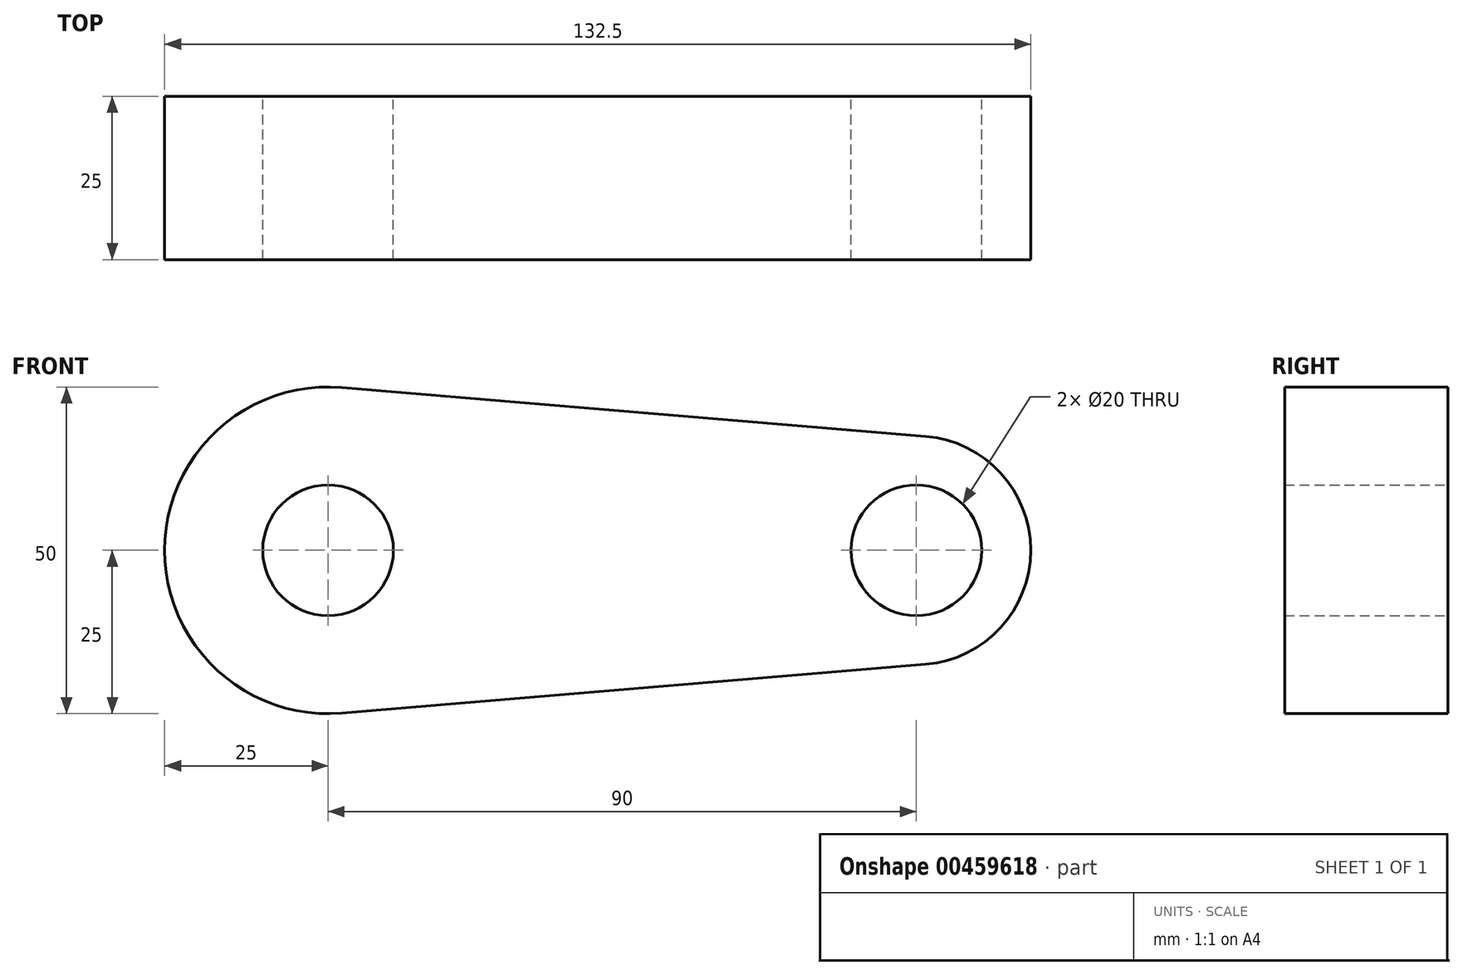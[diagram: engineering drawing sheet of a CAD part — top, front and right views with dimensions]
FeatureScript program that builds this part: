
annotation { "Feature Type Name" : "Feature", "Feature Type Description" : "" }
export const myFeature = defineFeature(function(context is Context, id is Id, definition is map)
    precondition{}
    {
        {
            var Q0;
            Q0=qCreatedBy(makeId("Front.planeOp"),FACE);
            var sketch = newSketch(context, id + "F0", { "sketchPlane" : qUnion([Q0])});
            skCircle(sketch, "E0", {"center": v(0, 0) * mm, "radius": 25 * mm});
            skCircle(sketch, "E1", {"center": v(90, 0) * mm, "radius": 17.5 * mm});
            skLineSegment(sketch, "E2", {"start": v(2.08, 24.91) * mm, "end": v(91.46, 17.44) * mm});
            skLineSegment(sketch, "E3", {"start": v(2.08, -24.91) * mm, "end": v(91.46, -17.44) * mm});
            skCircle(sketch, "E4", {"center": v(0, 0) * mm, "radius": 10 * mm});
            skCircle(sketch, "E5", {"center": v(90, 0) * mm, "radius": 10 * mm});
            skSolve(sketch);
        }
        {
            var Q0;
            Q0=makeQuery(id+"F0.imprint","IMPRINT",FACE,{"disambiguationData":[TD([[makeQuery(id+"F0.imprint","IMPRINT",EDGE,{"derivedFrom":sQuery(id+"F0.wireOp",EDGE,"E5")}),-1.0]])]});
            var Q1;
            {var subQ0=sQuery(id+"F0.wireOp",EDGE,"E2");Q1=makeQuery(id+"F0.imprint","IMPRINT",FACE,{"disambiguationData":[TD([[makeQuery(id+"F0.imprint","IMPRINT",EDGE,{"derivedFrom":subQ0}),-1.0]])]});}
            var Q2;
            Q2=makeQuery(id+"F0.imprint","IMPRINT",FACE,{"disambiguationData":[TD([[makeQuery(id+"F0.imprint","IMPRINT",EDGE,{"derivedFrom":sQuery(id+"F0.wireOp",EDGE,"E4")}),-1.0]])]});
            extrude(context, id + "F1", {"entities" : qUnion([Q0, Q1, Q2]), "depth" : 25 * mm});
        }
    });
